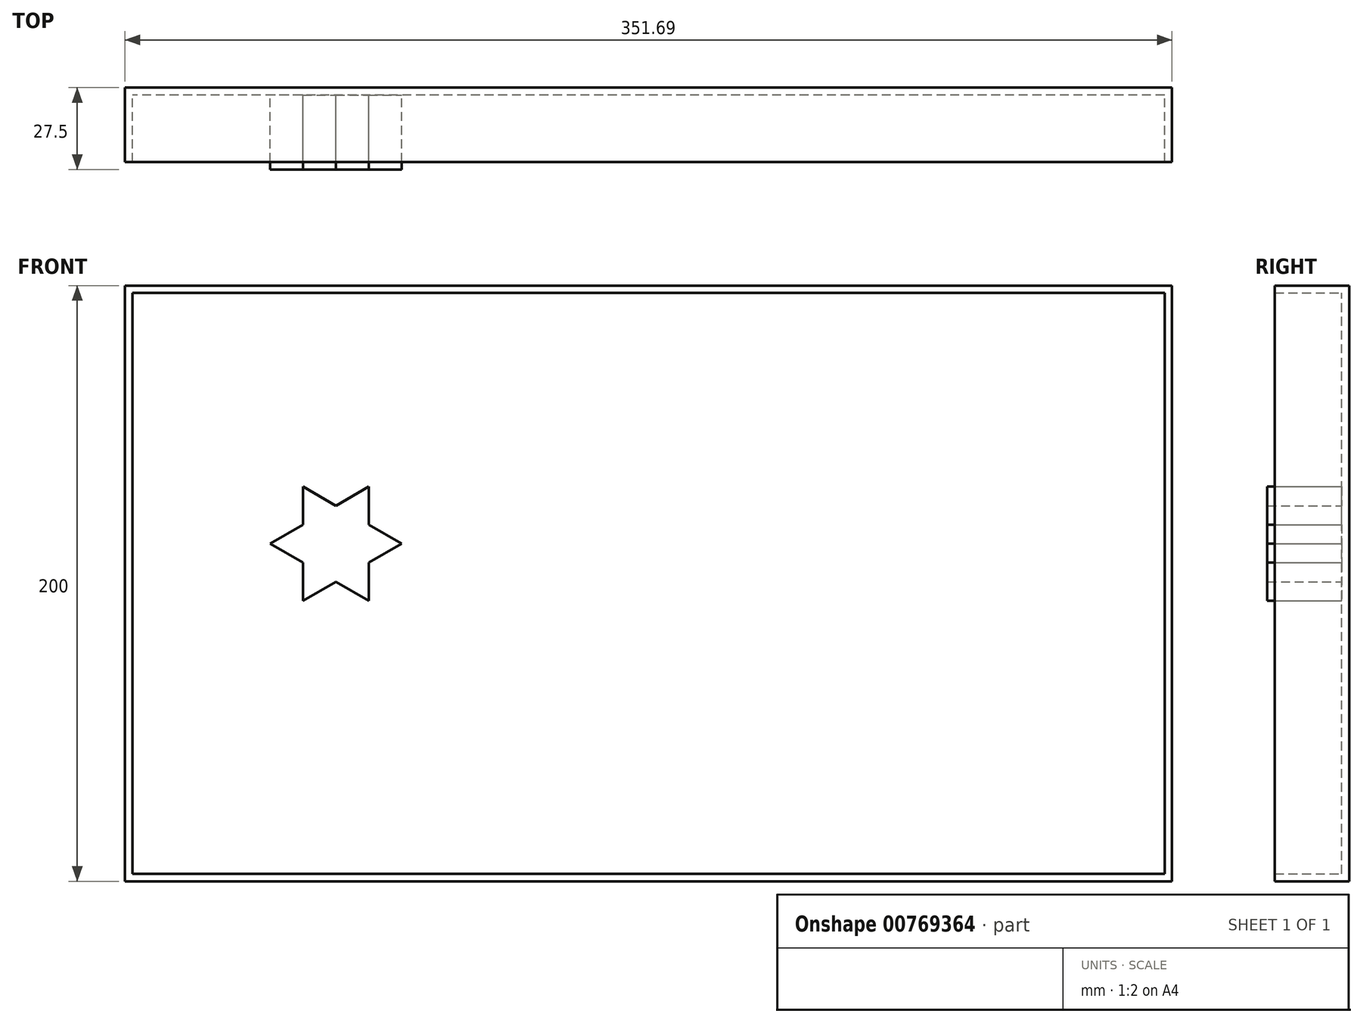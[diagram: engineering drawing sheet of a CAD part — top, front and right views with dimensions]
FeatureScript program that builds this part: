
annotation { "Feature Type Name" : "Feature", "Feature Type Description" : "" }
export const myFeature = defineFeature(function(context is Context, id is Id, definition is map)
    precondition{}
    {
        {
            var Q0;
            Q0=qCreatedBy(makeId("Front.planeOp"),FACE);
            var sketch = newSketch(context, id + "F0", { "sketchPlane" : qUnion([Q0])});
            skLineSegment(sketch, "E0.bottom", {"start": v(0, 0) * mm, "end": v(-351.69, 0) * mm});
            skLineSegment(sketch, "E0.top", {"start": v(0, 200) * mm, "end": v(-351.69, 200) * mm});
            skLineSegment(sketch, "E0.left", {"start": v(0, 0) * mm, "end": v(0, 200) * mm});
            skLineSegment(sketch, "E0.right", {"start": v(-351.69, 0) * mm, "end": v(-351.69, 200) * mm});
            skSolve(sketch);
        }
        {
            var Q0;
            Q0=makeQuery(id+"F0.imprint","IMPRINT",FACE,{"disambiguationData":[TD([[makeQuery(id+"F0.imprint","IMPRINT",EDGE,{"derivedFrom":sQuery(id+"F0.wireOp",EDGE,"E0.bottom")}),-1.0]])]});
            extrude(context, id + "F1", {"entities" : qUnion([Q0]), "depth" : 25 * mm, "offsetDistance" : 25 * mm});
        }
        {
            var Q0;
            Q0=makeQuery(id+"F1.opExtrude","CAP_FACE",FACE,{"disambiguationData":[OSD([sQuery(id+"F0.wireOp",EDGE,"E0.bottom"),sQuery(id+"F0.wireOp",EDGE,"E0.top"),sQuery(id+"F0.wireOp",EDGE,"E0.left"),sQuery(id+"F0.wireOp",EDGE,"E0.right")])],"isStart":false});
            shell(context, id + "F2", {"entities" : qUnion([Q0]), "thickness" : 2.5 * mm});
        }
        {
            var Q0;
            Q0=makeQuery(id+"F2.opShell","OFFSET_FACE",FACE,{"disambiguationData":[OSD([sQuery(id+"F0.wireOp",EDGE,"E0.bottom"),sQuery(id+"F0.wireOp",EDGE,"E0.top"),sQuery(id+"F0.wireOp",EDGE,"E0.left"),sQuery(id+"F0.wireOp",EDGE,"E0.right")])]});
            var sketch = newSketch(context, id + "F3", { "sketchPlane" : qUnion([Q0])});
            skCircle(sketch, "E1.cCircle", {"center": v(-280.87, 113.35) * mm, "radius": 11.07 * mm, "construction": true});
            skLineSegment(sketch, "E1.0", {"start": v(-269.8, 132.51) * mm, "end": v(-269.8, 94.18) * mm});
            skLineSegment(sketch, "E1.1", {"start": v(-269.8, 94.18) * mm, "end": v(-303, 113.35) * mm});
            skLineSegment(sketch, "E1.2", {"start": v(-303, 113.35) * mm, "end": v(-269.8, 132.51) * mm});
            skPoint(sketch, "E1.0.midPoint", {"position": v(-269.8, 113.35) * mm});
            skLineSegment(sketch, "E2.0", {"start": v(-291.94, 132.51) * mm, "end": v(-258.74, 113.35) * mm});
            skLineSegment(sketch, "E2.1", {"start": v(-258.74, 113.35) * mm, "end": v(-291.94, 94.18) * mm});
            skLineSegment(sketch, "E2.2", {"start": v(-291.94, 94.18) * mm, "end": v(-291.94, 132.51) * mm});
            skPoint(sketch, "E2.0.midPoint", {"position": v(-275.34, 122.93) * mm});
            skSolve(sketch);
        }
        {
            var Q0;
            {var subQ0=sQuery(id+"F3.wireOp",EDGE,"E2.2");var subQ1=sQuery(id+"F3.wireOp",EDGE,"E1.2");var subQ2=makeQuery(id+"F3.imprint","INTERSECT",VERTEX,{"derivedFrom":[subQ1,subQ0]});Q0=makeQuery(id+"F3.imprint","IMPRINT",FACE,{"disambiguationData":[TD([[makeQuery(id+"F3.imprint","IMPRINT",EDGE,{"disambiguationData":[TD([[subQ2,-1.0]])],"derivedFrom":subQ1}),1.0]])]});}
            var Q1;
            {var subQ0=sQuery(id+"F3.wireOp",EDGE,"E2.0");var subQ1=sQuery(id+"F3.wireOp",EDGE,"E1.0");var subQ2=makeQuery(id+"F3.imprint","INTERSECT",VERTEX,{"derivedFrom":[subQ1,subQ0]});Q1=makeQuery(id+"F3.imprint","IMPRINT",FACE,{"disambiguationData":[TD([[makeQuery(id+"F3.imprint","IMPRINT",EDGE,{"disambiguationData":[TD([[subQ2,-1.0]])],"derivedFrom":subQ1}),-1.0]])]});}
            var Q2;
            {var subQ0=sQuery(id+"F3.wireOp",EDGE,"E1.2");var subQ1=sQuery(id+"F3.wireOp",EDGE,"E1.0");var subQ2=makeQuery(id+"F3.imprint","INTERSECT",VERTEX,{"derivedFrom":[subQ1,subQ0]});Q2=makeQuery(id+"F3.imprint","IMPRINT",FACE,{"disambiguationData":[TD([[makeQuery(id+"F3.imprint","IMPRINT",EDGE,{"disambiguationData":[TD([[subQ2,-1.0]])],"derivedFrom":subQ1}),-1.0]])]});}
            var Q3;
            {var subQ0=sQuery(id+"F3.wireOp",EDGE,"E1.1");var subQ1=sQuery(id+"F3.wireOp",EDGE,"E1.0");var subQ2=makeQuery(id+"F3.imprint","INTERSECT",VERTEX,{"derivedFrom":[subQ1,subQ0]});Q3=makeQuery(id+"F3.imprint","IMPRINT",FACE,{"disambiguationData":[TD([[makeQuery(id+"F3.imprint","IMPRINT",EDGE,{"disambiguationData":[TD([[subQ2,1.0]])],"derivedFrom":subQ1}),-1.0]])]});}
            var Q4;
            {var subQ0=sQuery(id+"F3.wireOp",EDGE,"E2.1");var subQ1=sQuery(id+"F3.wireOp",EDGE,"E1.1");var subQ2=makeQuery(id+"F3.imprint","INTERSECT",VERTEX,{"derivedFrom":[subQ1,subQ0]});Q4=makeQuery(id+"F3.imprint","IMPRINT",FACE,{"disambiguationData":[TD([[makeQuery(id+"F3.imprint","IMPRINT",EDGE,{"disambiguationData":[TD([[subQ2,-1.0]])],"derivedFrom":subQ1}),1.0]])]});}
            var Q5;
            {var subQ0=sQuery(id+"F3.wireOp",EDGE,"E1.2");var subQ1=sQuery(id+"F3.wireOp",EDGE,"E1.1");var subQ2=makeQuery(id+"F3.imprint","INTERSECT",VERTEX,{"derivedFrom":[subQ1,subQ0]});Q5=makeQuery(id+"F3.imprint","IMPRINT",FACE,{"disambiguationData":[TD([[makeQuery(id+"F3.imprint","IMPRINT",EDGE,{"disambiguationData":[TD([[subQ2,1.0]])],"derivedFrom":subQ1}),-1.0]])]});}
            var Q6;
            {var subQ0=sQuery(id+"F3.wireOp",EDGE,"E2.0");var subQ1=sQuery(id+"F3.wireOp",EDGE,"E1.0");var subQ2=makeQuery(id+"F3.imprint","INTERSECT",VERTEX,{"derivedFrom":[subQ1,subQ0]});Q6=makeQuery(id+"F3.imprint","IMPRINT",FACE,{"disambiguationData":[TD([[makeQuery(id+"F3.imprint","IMPRINT",EDGE,{"disambiguationData":[TD([[subQ2,-1.0]])],"derivedFrom":subQ1}),1.0]])]});}
            extrude(context, id + "F4", {"entities" : qUnion([Q0, Q1, Q2, Q3, Q4, Q5, Q6]), "operationType" : NewBodyOperationType.ADD, "depth" : 25 * mm, "offsetDistance" : 25 * mm});
        }
    });
